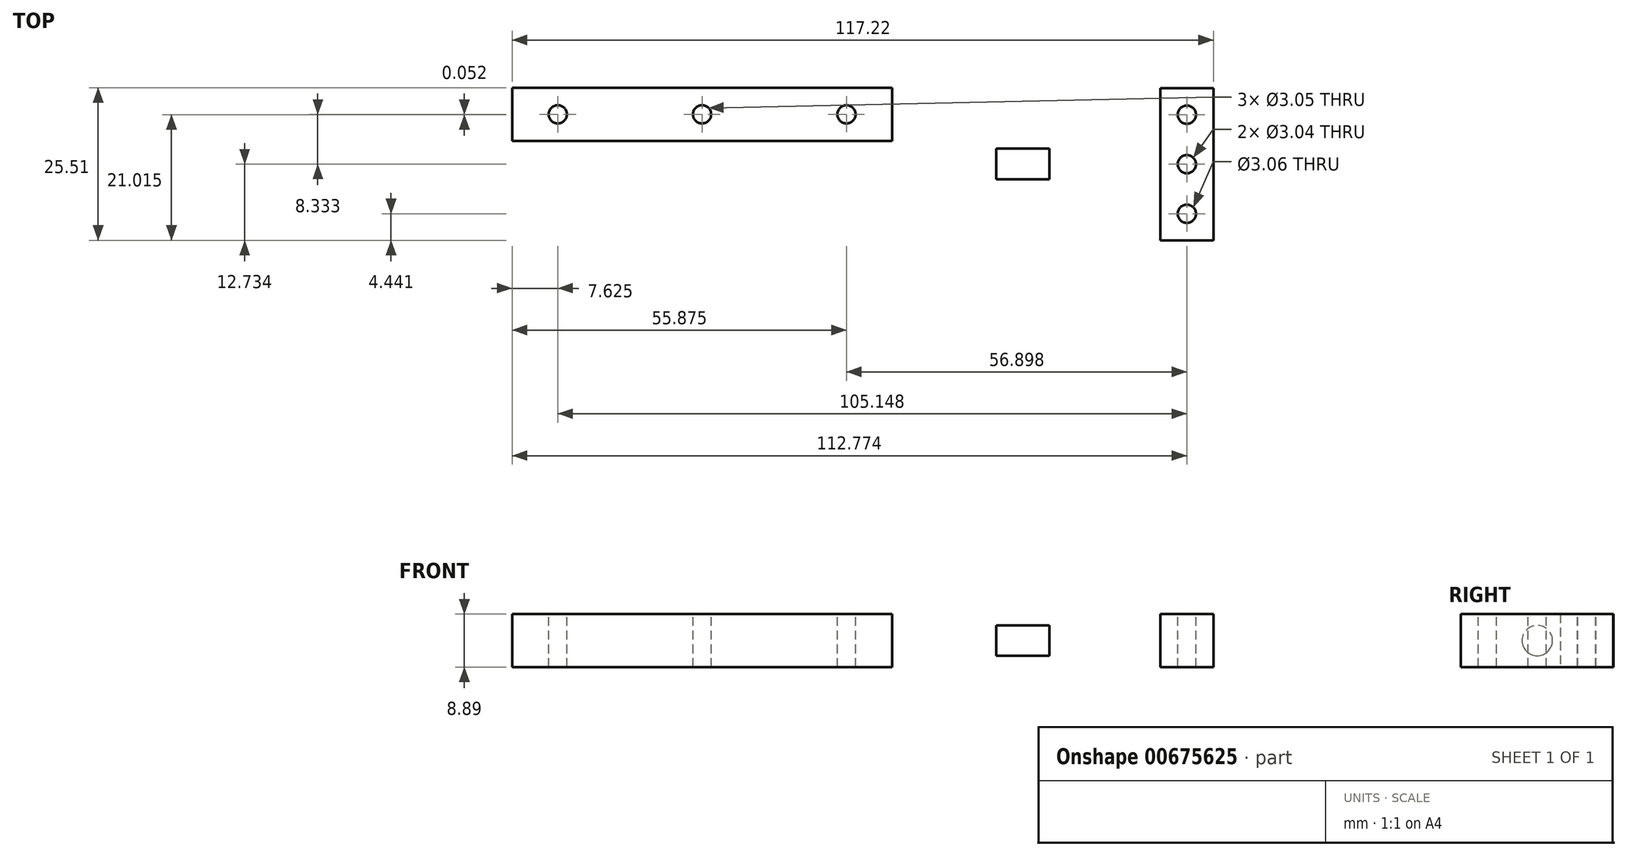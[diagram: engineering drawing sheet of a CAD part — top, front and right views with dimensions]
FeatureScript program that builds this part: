
annotation { "Feature Type Name" : "Feature", "Feature Type Description" : "" }
export const myFeature = defineFeature(function(context is Context, id is Id, definition is map)
    precondition{}
    {
        {
            var Q0;
            Q0=qCreatedBy(makeId("Top.planeOp"),FACE);
            var sketch = newSketch(context, id + "F0", { "sketchPlane" : qUnion([Q0])});
            skLineSegment(sketch, "E0", {"start": v(-73.93, 0) * mm, "end": v(-10.43, 0) * mm});
            skLineSegment(sketch, "E1", {"start": v(-10.43, 0) * mm, "end": v(-10.43, -8.89) * mm});
            skLineSegment(sketch, "E2", {"start": v(-73.93, -8.89) * mm, "end": v(-73.93, 0) * mm});
            skLineSegment(sketch, "E3", {"start": v(-10.43, -8.89) * mm, "end": v(-73.93, -8.89) * mm});
            skSolve(sketch);
        }
        {
            var Q0;
            Q0=makeQuery(id+"F0.imprint","IMPRINT",FACE,{"disambiguationData":[TD([[makeQuery(id+"F0.imprint","IMPRINT",EDGE,{"derivedFrom":sQuery(id+"F0.wireOp",EDGE,"E0")}),-1.0]])]});
            extrude(context, id + "F1", {"entities" : qUnion([Q0]), "depth" : 8.9 * mm, "offsetDistance" : 25.4 * mm});
        }
        {
            var Q0;
            Q0=makeQuery(id+"F1.opExtrude","CAP_FACE",FACE,{"disambiguationData":[OSD([sQuery(id+"F0.wireOp",EDGE,"E0"),sQuery(id+"F0.wireOp",EDGE,"E1"),sQuery(id+"F0.wireOp",EDGE,"E2"),sQuery(id+"F0.wireOp",EDGE,"E3")])],"isStart":false});
            var sketch = newSketch(context, id + "F2", { "sketchPlane" : qUnion([Q0])});
            skLineSegment(sketch, "E4", {"start": v(-73.93, -4.44) * mm, "end": v(-66.3, -4.44) * mm});
            skLineSegment(sketch, "E5", {"start": v(-10.43, -4.44) * mm, "end": v(-18.05, -4.44) * mm});
            skCircle(sketch, "E6", {"center": v(-66.3, -4.44) * mm, "radius": 1.53 * mm});
            skCircle(sketch, "E7", {"center": v(-18.05, -4.44) * mm, "radius": 1.52 * mm});
            skSolve(sketch);
        }
        {
            var Q0;
            Q0=makeQuery(id+"F1.opExtrude","CAP_FACE",FACE,{"disambiguationData":[OSD([sQuery(id+"F0.wireOp",EDGE,"E0"),sQuery(id+"F0.wireOp",EDGE,"E1"),sQuery(id+"F0.wireOp",EDGE,"E2"),sQuery(id+"F0.wireOp",EDGE,"E3")])],"isStart":false});
            var sketch = newSketch(context, id + "F3", { "sketchPlane" : qUnion([Q0])});
            skLineSegment(sketch, "E8", {"start": v(-73.93, -4.44) * mm, "end": v(-42.2, -4.44) * mm});
            skCircle(sketch, "E9", {"center": v(-42.2, -4.44) * mm, "radius": 1.52 * mm});
            skSolve(sketch);
        }
        {
            var Q0;
            Q0=qCreatedBy(makeId("Top.planeOp"),FACE);
            var sketch = newSketch(context, id + "F4", { "sketchPlane" : qUnion([Q0])});
            skLineSegment(sketch, "E10", {"start": v(15.86, 0) * mm, "end": v(15.86, -25.47) * mm});
            skLineSegment(sketch, "E11", {"start": v(15.86, -25.47) * mm, "end": v(6.97, -25.47) * mm});
            skLineSegment(sketch, "E12", {"start": v(6.97, -25.47) * mm, "end": v(6.97, 0) * mm});
            skLineSegment(sketch, "E13", {"start": v(6.97, 0) * mm, "end": v(15.86, 0) * mm});
            skSolve(sketch);
        }
        {
            var Q0;
            Q0=makeQuery(id+"F4.imprint","IMPRINT",FACE,{"disambiguationData":[TD([[makeQuery(id+"F4.imprint","IMPRINT",EDGE,{"derivedFrom":sQuery(id+"F4.wireOp",EDGE,"E10")}),-1.0]])]});
            extrude(context, id + "F5", {"entities" : qUnion([Q0]), "depth" : 8.9 * mm, "offsetDistance" : 25.4 * mm});
        }
        {
            var Q0;
            Q0=makeQuery(id+"F5.opExtrude","CAP_FACE",FACE,{"disambiguationData":[OSD([sQuery(id+"F4.wireOp",EDGE,"E10"),sQuery(id+"F4.wireOp",EDGE,"E11"),sQuery(id+"F4.wireOp",EDGE,"E12"),sQuery(id+"F4.wireOp",EDGE,"E13")])],"isStart":false});
            var sketch = newSketch(context, id + "F6", { "sketchPlane" : qUnion([Q0])});
            skLineSegment(sketch, "E14", {"start": v(11.42, 0) * mm, "end": v(11.42, -8.9) * mm});
            skLineSegment(sketch, "E15", {"start": v(11.42, -25.47) * mm, "end": v(11.42, -16.59) * mm});
            skLineSegment(sketch, "E16", {"start": v(11.42, -16.59) * mm, "end": v(11.42, -21.03) * mm});
            skLineSegment(sketch, "E17", {"start": v(11.42, 0) * mm, "end": v(11.42, -4.45) * mm});
            skCircle(sketch, "E18", {"center": v(11.42, -4.45) * mm, "radius": 1.52 * mm});
            skCircle(sketch, "E19", {"center": v(11.42, -21.03) * mm, "radius": 1.52 * mm});
            skSolve(sketch);
        }
        {
            var Q0;
            {var subQ0=sQuery(id+"F6.wireOp",EDGE,"E16");var subQ1=sQuery(id+"F6.wireOp",EDGE,"E15");var subQ2=makeQuery(id+"F6.imprint","INTERSECT",VERTEX,{"derivedFrom":[subQ1,subQ0]});Q0=makeQuery(id+"F6.imprint","IMPRINT",FACE,{"disambiguationData":[TD([[makeQuery(id+"F6.imprint","IMPRINT",EDGE,{"disambiguationData":[TD([[subQ2,1.0]])],"derivedFrom":subQ1}),1.0]])]});}
            var Q1;
            {var subQ0=sQuery(id+"F6.wireOp",EDGE,"E16");var subQ1=sQuery(id+"F6.wireOp",EDGE,"E15");var subQ2=makeQuery(id+"F6.imprint","INTERSECT",VERTEX,{"derivedFrom":[subQ1,subQ0]});Q1=makeQuery(id+"F6.imprint","IMPRINT",FACE,{"disambiguationData":[TD([[makeQuery(id+"F6.imprint","IMPRINT",EDGE,{"disambiguationData":[TD([[subQ2,1.0]])],"derivedFrom":subQ1}),-1.0]])]});}
            var Q2;
            {var subQ0=sQuery(id+"F6.wireOp",EDGE,"E17");var subQ1=sQuery(id+"F6.wireOp",EDGE,"E14");var subQ2=makeQuery(id+"F6.imprint","INTERSECT",VERTEX,{"derivedFrom":[subQ1,subQ0]});Q2=makeQuery(id+"F6.imprint","IMPRINT",FACE,{"disambiguationData":[TD([[makeQuery(id+"F6.imprint","IMPRINT",EDGE,{"disambiguationData":[TD([[subQ2,-1.0]])],"derivedFrom":subQ1}),-1.0]])]});}
            var Q3;
            {var subQ0=sQuery(id+"F6.wireOp",EDGE,"E17");var subQ1=sQuery(id+"F6.wireOp",EDGE,"E14");var subQ2=makeQuery(id+"F6.imprint","INTERSECT",VERTEX,{"derivedFrom":[subQ1,subQ0]});Q3=makeQuery(id+"F6.imprint","IMPRINT",FACE,{"disambiguationData":[TD([[makeQuery(id+"F6.imprint","IMPRINT",EDGE,{"disambiguationData":[TD([[subQ2,-1.0]])],"derivedFrom":subQ1}),1.0]])]});}
            extrude(context, id + "F7", {"entities" : qUnion([Q0, Q1, Q2, Q3]), "operationType" : NewBodyOperationType.REMOVE, "oppositeDirection" : true, "depth" : 12.7 * mm, "offsetDistance" : 25.4 * mm});
        }
        {
            var Q0;
            Q0=makeQuery(id+"F5.opExtrude","SWEPT_FACE",FACE,{"disambiguationData":[OSD([sQuery(id+"F4.wireOp",EDGE,"E10")])]});
            var sketch = newSketch(context, id + "F8", { "sketchPlane" : qUnion([Q0])});
            skLineSegment(sketch, "E20", {"start": v(-25.47, 4.44) * mm, "end": v(0, 4.45) * mm});
            skLineSegment(sketch, "E21", {"start": v(0, 4.45) * mm, "end": v(-12.74, 4.45) * mm});
            skCircle(sketch, "E22", {"center": v(-12.74, 4.45) * mm, "radius": 2.54 * mm});
            skSolve(sketch);
        }
        {
            var Q0;
            {var subQ0=sQuery(id+"F8.wireOp",EDGE,"E21");var subQ1=sQuery(id+"F8.wireOp",EDGE,"E20");var subQ2=makeQuery(id+"F8.imprint","INTERSECT",VERTEX,{"derivedFrom":[subQ1,subQ0]});Q0=makeQuery(id+"F8.imprint","IMPRINT",FACE,{"disambiguationData":[TD([[makeQuery(id+"F8.imprint","IMPRINT",EDGE,{"disambiguationData":[TD([[subQ2,1.0]])],"derivedFrom":subQ1}),-1.0]])]});}
            var Q1;
            {var subQ0=sQuery(id+"F8.wireOp",EDGE,"E21");var subQ1=sQuery(id+"F8.wireOp",EDGE,"E20");var subQ2=makeQuery(id+"F8.imprint","INTERSECT",VERTEX,{"derivedFrom":[subQ1,subQ0]});Q1=makeQuery(id+"F8.imprint","IMPRINT",FACE,{"disambiguationData":[TD([[makeQuery(id+"F8.imprint","IMPRINT",EDGE,{"disambiguationData":[TD([[subQ2,1.0]])],"derivedFrom":subQ1}),1.0]])]});}
            extrude(context, id + "F9", {"entities" : qUnion([Q0, Q1]), "operationType" : NewBodyOperationType.REMOVE, "oppositeDirection" : true, "depth" : 25.4 * mm, "offsetDistance" : 25.4 * mm});
        }
        {
            var Q0;
            Q0=qCreatedBy(makeId("Top.planeOp"),FACE);
            var sketch = newSketch(context, id + "F10", { "sketchPlane" : qUnion([Q0])});
            skLineSegment(sketch, "E23", {"start": v(43.29, -0.04) * mm, "end": v(43.29, -25.51) * mm});
            skLineSegment(sketch, "E24", {"start": v(43.29, -25.51) * mm, "end": v(34.4, -25.51) * mm});
            skLineSegment(sketch, "E25", {"start": v(34.4, -25.51) * mm, "end": v(34.4, -0.04) * mm});
            skLineSegment(sketch, "E26", {"start": v(34.4, -0.04) * mm, "end": v(43.29, -0.04) * mm});
            skSolve(sketch);
        }
        {
            var Q0;
            Q0=makeQuery(id+"F10.imprint","IMPRINT",FACE,{"disambiguationData":[TD([[makeQuery(id+"F10.imprint","IMPRINT",EDGE,{"derivedFrom":sQuery(id+"F10.wireOp",EDGE,"E23")}),-1.0]])]});
            extrude(context, id + "F11", {"entities" : qUnion([Q0]), "depth" : 8.9 * mm, "offsetDistance" : 25.4 * mm});
        }
        {
            var Q0;
            Q0=makeQuery(id+"F11.opExtrude","CAP_FACE",FACE,{"disambiguationData":[OSD([sQuery(id+"F10.wireOp",EDGE,"E23"),sQuery(id+"F10.wireOp",EDGE,"E24"),sQuery(id+"F10.wireOp",EDGE,"E25"),sQuery(id+"F10.wireOp",EDGE,"E26")])],"isStart":false});
            var sketch = newSketch(context, id + "F12", { "sketchPlane" : qUnion([Q0])});
            skLineSegment(sketch, "E27", {"start": v(38.84, -0.04) * mm, "end": v(38.84, -4.5) * mm});
            skLineSegment(sketch, "E28", {"start": v(38.84, -25.51) * mm, "end": v(38.84, -21.07) * mm});
            skLineSegment(sketch, "E29", {"start": v(43.29, -12.78) * mm, "end": v(38.84, -12.78) * mm});
            skCircle(sketch, "E30", {"center": v(38.84, -4.5) * mm, "radius": 1.53 * mm});
            skCircle(sketch, "E31", {"center": v(38.84, -12.78) * mm, "radius": 1.52 * mm});
            skCircle(sketch, "E32", {"center": v(38.84, -21.07) * mm, "radius": 1.53 * mm});
            skSolve(sketch);
        }
        {
            var Q0;
            Q0=makeQuery(id+"F2.imprint","IMPRINT",FACE,{"disambiguationData":[TD([[makeQuery(id+"F2.imprint","IMPRINT",EDGE,{"derivedFrom":sQuery(id+"F2.wireOp",EDGE,"E6")}),1.0]])]});
            var Q1;
            Q1=makeQuery(id+"F2.imprint","IMPRINT",FACE,{"disambiguationData":[TD([[makeQuery(id+"F2.imprint","IMPRINT",EDGE,{"derivedFrom":sQuery(id+"F2.wireOp",EDGE,"E7")}),1.0]])]});
            extrude(context, id + "F13", {"entities" : qUnion([Q0, Q1]), "operationType" : NewBodyOperationType.REMOVE, "oppositeDirection" : true, "depth" : 25.4 * mm, "offsetDistance" : 25.4 * mm});
        }
        {
            var Q0;
            Q0=makeQuery(id+"F3.imprint","IMPRINT",FACE,{"disambiguationData":[TD([[makeQuery(id+"F3.imprint","IMPRINT",EDGE,{"derivedFrom":sQuery(id+"F3.wireOp",EDGE,"E9")}),1.0]])]});
            extrude(context, id + "F14", {"entities" : qUnion([Q0]), "operationType" : NewBodyOperationType.REMOVE, "oppositeDirection" : true, "depth" : 25.4 * mm, "offsetDistance" : 25.4 * mm});
        }
        {
            var Q0;
            Q0=makeQuery(id+"F12.imprint","IMPRINT",FACE,{"disambiguationData":[TD([[makeQuery(id+"F12.imprint","IMPRINT",EDGE,{"derivedFrom":sQuery(id+"F12.wireOp",EDGE,"E32")}),1.0]])]});
            var Q1;
            Q1=makeQuery(id+"F12.imprint","IMPRINT",FACE,{"disambiguationData":[TD([[makeQuery(id+"F12.imprint","IMPRINT",EDGE,{"derivedFrom":sQuery(id+"F12.wireOp",EDGE,"E31")}),1.0]])]});
            var Q2;
            Q2=makeQuery(id+"F12.imprint","IMPRINT",FACE,{"disambiguationData":[TD([[makeQuery(id+"F12.imprint","IMPRINT",EDGE,{"derivedFrom":sQuery(id+"F12.wireOp",EDGE,"E30")}),1.0]])]});
            extrude(context, id + "F15", {"entities" : qUnion([Q0, Q1, Q2]), "operationType" : NewBodyOperationType.REMOVE, "oppositeDirection" : true, "depth" : 25.4 * mm, "offsetDistance" : 25.4 * mm});
        }
    });
